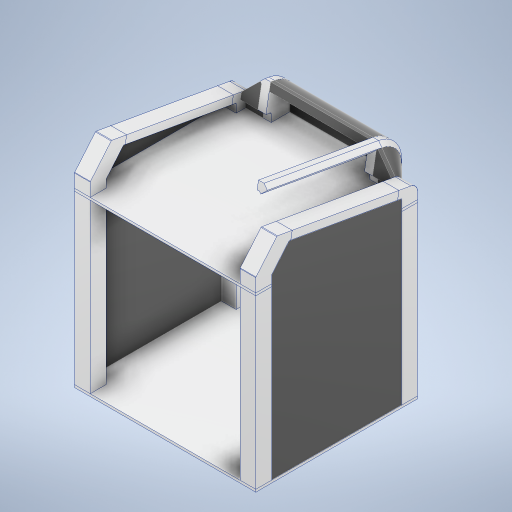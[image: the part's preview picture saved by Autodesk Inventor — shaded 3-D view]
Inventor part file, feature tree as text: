
AUTODESK INVENTOR PART (.ipt)
format: ipt  version: 2024 (Build 280153000, 153)  size: 913,920 bytes
history: native  units: mm
features: projected_geometry x29, sketch x20, extrude x20, other x11, mirror x6, fillet x5, revolve x3, plane x2
ambient origin geometry x8: Origin, YZ Plane, XZ Plane, XY Plane, X Axis, Y Axis, Z Axis, Center Point
bodies: Solid1 (feature_tree)
feature tree (96):
  sketch  "Sketch1"  dims[d0=460.0mm d1=410.0mm]
  extrude  "Extrusion1"  Depth=410.0mm
  revolve  "Revolution1"  [1 undecoded]
  sketch  "Sketch3"  dims[d4=135.0deg d5=135.0deg]
  plane  "Work Plane4"
  extrude  "Extrusion5"  TaperAngle=135.0deg  [1 undecoded]
  extrude  "Extrusion6"  Depth=20.0mm
  fillet  "Fillet1"  Radius=13.962634mm
  fillet  "Fillet3"  [1 undecoded]
  fillet  "Fillet4"  Radius=10.0mm
  fillet  "Fillet5"  Radius=10.0mm
  extrude  "Extrusion7"  Depth=2.0mm
  sketch  "Sketch8"  dims[d25=2.0mm d27=2.0mm]
  extrude  "Extrusion8"  Depth=2.0mm
  extrude  "Extrusion9"  Depth=10.0mm
  sketch  "Sketch10"  dims[d30=67.5deg d32=10.0mm]
  extrude  "Extrusion10"  Depth=40.0mm
  mirror  "Mirror1"
  extrude  "Extrusion11"  Depth=40.0mm
  mirror  "Mirror2"
  extrude  "Extrusion12"  Depth=250.0mm
  mirror  "Mirror3"
  extrude  "Extrusion13"  Depth=40.0mm
  mirror  "Mirror4"
  sketch  "Sketch14"  dims[d38=250.0mm d39=60.0mm]
  extrude  "Extrusion14"  Depth=40.0mm
  extrude  "Extrusion15"  Depth=40.0mm
  extrude  "Extrusion16"  Depth=40.0mm
  extrude  "Extrusion17"  Depth=10.0mm
  extrude  "Extrusion18"  Depth=26.0mm
  revolve  "Revolution2"  [1 undecoded]
  extrude  "Extrusion19"  Depth=105.0mm
  mirror  "Mirror5"
  extrude  "Extrusion20"  Depth=220.0mm
  fillet  "Fillet6"  Radius=8.0mm
  extrude  "Extrusion21"  Depth=55.0mm
  revolve  "Revolution3"  Angle=150.0deg
  extrude  "Extrusion22"  Depth=55.0mm
  mirror  "Mirror6"
  extrude  "Extrusion23"  Depth=425.0mm TaperAngle=0.0deg
  sketch  "Sketch2"  dims[d2=40.0mm d3=40.0mm]
  projected_geometry  "Projected Loop1"
  projected_geometry  "Projected Loop2"
  plane  "Work Plane3"
  sketch  "Sketch6"  dims[d7=450.0mm d8=0.0mm d9=20.0mm d10=13.962634mm d20=-10.0mm d21=10.0mm d22=0.0mm d23=10.0mm d24=0.0mm]
  projected_geometry  "Projected Loop4"
  other  "Base Plate"
  projected_geometry  "Projected Loop5"
  other  "Verticals"
  sketch  "Sketch9"  dims[d28=2.0mm d29=2.0mm]
  projected_geometry  "Projected Loop6"
  other  "Gantry Plate"
  projected_geometry  "Projected Loop7"
  projected_geometry  "Projected Loop8"
  projected_geometry  "Projected Loop9"
  projected_geometry  "Projected Loop10"
  projected_geometry  "Projected Loop11"
  projected_geometry  "Projected Loop12"
  other  "Printed Top Bar Holders"
  other  "Top Bars"
  sketch  "Sketch12"  dims[d34=50.857864mm d35=40.0mm]
  projected_geometry  "Projected Loop13"
  projected_geometry  "Projected Loop14"
  projected_geometry  "Projected Loop15"
  sketch  "Sketch13"  dims[d36=40.0mm d37=300.0mm]
  other  "Side Shear Panels"
  other  "Rear Curve Panel"
  sketch  "Sketch15"  dims[d40=40.0mm d41=40.0mm]
  projected_geometry  "Projected Loop16"
  projected_geometry  "Projected Loop17"
  projected_geometry  "Projected Loop18"
  sketch  "Sketch16"  dims[d42=40.0mm d43=40.0mm]
  projected_geometry  "Projected Loop19"
  projected_geometry  "Projected Loop20"
  other  "Rear Shear Panel"
  sketch  "Sketch17"  dims[d44=40.0mm d45=40.0mm]
  projected_geometry  "Projected Loop21"
  projected_geometry  "Projected Loop22"
  other  "Rear Line Panel"
  sketch  "Sketch18"  dims[d46=80.0mm d47=40.0mm]
  projected_geometry  "Projected Loop23"
  sketch  "Sketch19"  dims[d48=10.0mm d50=10.0mm]
  projected_geometry  "Projected Loop24"
  sketch  "Sketch20"  dims[d51=3.0mm d52=26.0mm]
  other  "Rear Vertical Panels"
  sketch  "Sketch21"  dims[d53=40.0mm d54=20.0mm]
  projected_geometry  "Projected Loop25"
  other  "Rear Corner Curves"
  sketch  "Sketch22"  dims[d55=55.0mm d56=105.0mm]
  projected_geometry  "Projected Loop26"
  sketch  "Sketch23"  dims[d57=90.0mm d58=220.0mm d59=8.0mm]
  projected_geometry  "Projected Loop27"
  sketch  "Sketch24"  dims[d60=20.0mm d61=55.0mm d62=150.0deg d63=6.35mm d64=0.0mm d65=55.0mm d66=425.0mm d67=0.0mm d68=6.35mm d69=0.0mm d70=20.0mm d71=40.0mm d72=20.0mm d73=2.0mm d77=275.0mm d78=40.0mm d79=0.0mm d80=40.0mm d81=0.0mm d82=3.5mm d83=0.0mm d85=3.175mm d86=0.0mm d88=10.0mm d89=20.0mm d90=3.175mm d91=0.0mm d92=10.0mm d93=0.0mm d94=3.5mm d95=0.0mm d96=0.5mm d97=3.175mm d98=0.0mm d99=5.0mm d100=18.65mm d101=0.0mm d102=13.962634mm d103=0.0mm d104=0.0mm d105=40.0mm d106=40.0mm d107=2.0mm d108=0.5mm d109=0.5mm d110=0.5mm d111=0.5mm d112=0.5mm d113=3.175mm d114=0.0mm d115=2.0mm d116=18.65mm d117=0.0mm d118=13.962634mm d119=18.65mm d120=0.0mm d121=20.0mm d122=20.0mm d123=285.0mm d124=0.0mm]
  projected_geometry  "Projected Loop28"
  projected_geometry  "Project Cut Edges1"
  projected_geometry  "Project Cut Edges2"
note: 4 required parameter values undecoded (feature->parameter linkage not recoverable at this tier; creation-order binding heuristic only, values carry confidence <= 0.55)